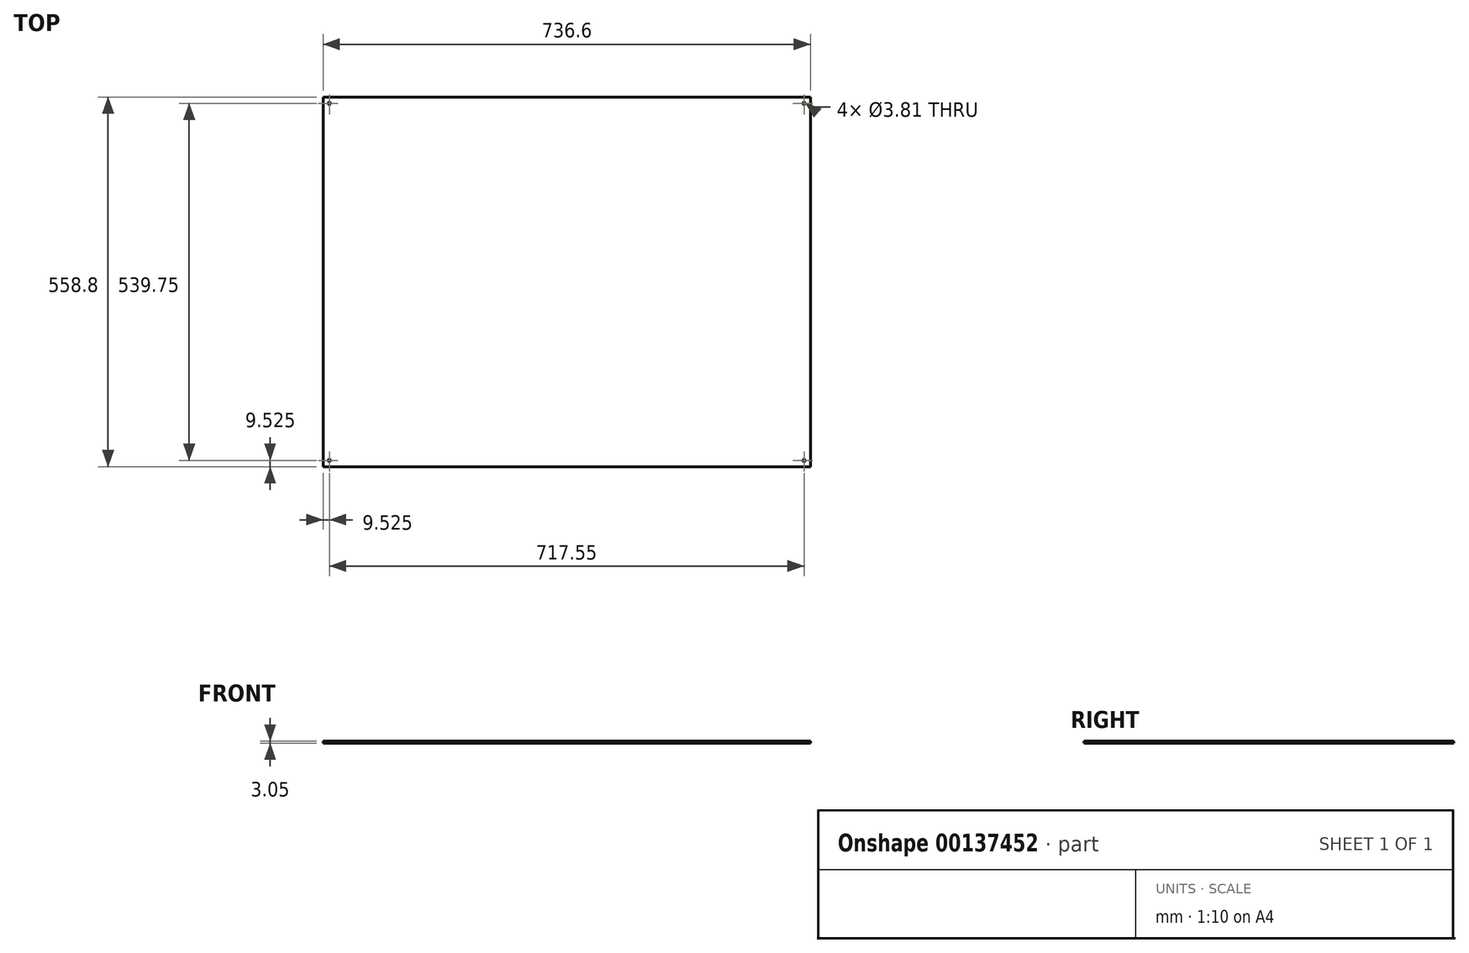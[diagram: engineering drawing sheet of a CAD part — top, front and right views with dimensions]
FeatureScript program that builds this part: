
annotation { "Feature Type Name" : "Feature", "Feature Type Description" : "" }
export const myFeature = defineFeature(function(context is Context, id is Id, definition is map)
    precondition{}
    {
        {
            var Q0;
            Q0=qCreatedBy(makeId("Top.planeOp"),FACE);
            var sketch = newSketch(context, id + "F0", { "sketchPlane" : qUnion([Q0])});
            skLineSegment(sketch, "E0.bottom", {"start": v(-368.3, 279.4) * mm, "end": v(368.3, 279.4) * mm});
            skLineSegment(sketch, "E0.top", {"start": v(-368.3, -279.4) * mm, "end": v(368.3, -279.4) * mm});
            skLineSegment(sketch, "E0.left", {"start": v(-368.3, 279.4) * mm, "end": v(-368.3, -279.4) * mm});
            skLineSegment(sketch, "E0.right", {"start": v(368.3, 279.4) * mm, "end": v(368.3, -279.4) * mm});
            skSolve(sketch);
        }
        {
            var Q0;
            Q0=qSketchRegion(id+"F0",true);
            extrude(context, id + "F1", {"entities" : qUnion([Q0]), "depth" : 3.05 * mm});
        }
        {
            var Q0;
            Q0=makeQuery(id+"F1.opExtrude","CAP_FACE",FACE,{"disambiguationData":[OSD([sQuery(id+"F0.wireOp",EDGE,"E0.bottom"),sQuery(id+"F0.wireOp",EDGE,"E0.top"),sQuery(id+"F0.wireOp",EDGE,"E0.left"),sQuery(id+"F0.wireOp",EDGE,"E0.right")])],"isStart":false});
            var sketch = newSketch(context, id + "F2", { "sketchPlane" : qUnion([Q0])});
            skCircle(sketch, "E1", {"center": v(-358.77, 269.88) * mm, "radius": 1.9 * mm});
            skCircle(sketch, "E2.MirrorC", {"center": v(358.77, 269.88) * mm, "radius": 1.9 * mm});
            skCircle(sketch, "E3.MirrorC", {"center": v(-358.77, -269.88) * mm, "radius": 1.9 * mm});
            skCircle(sketch, "E4.MirrorC", {"center": v(358.77, -269.88) * mm, "radius": 1.9 * mm});
            skSolve(sketch);
        }
        {
            var Q0;
            Q0=qSketchRegion(id+"F2",true);
            extrude(context, id + "F3", {"entities" : qUnion([Q0]), "operationType" : NewBodyOperationType.REMOVE, "endBound" : BoundingType.THROUGH_ALL, "oppositeDirection" : true, "depth" : 25.4 * mm});
        }
    });
